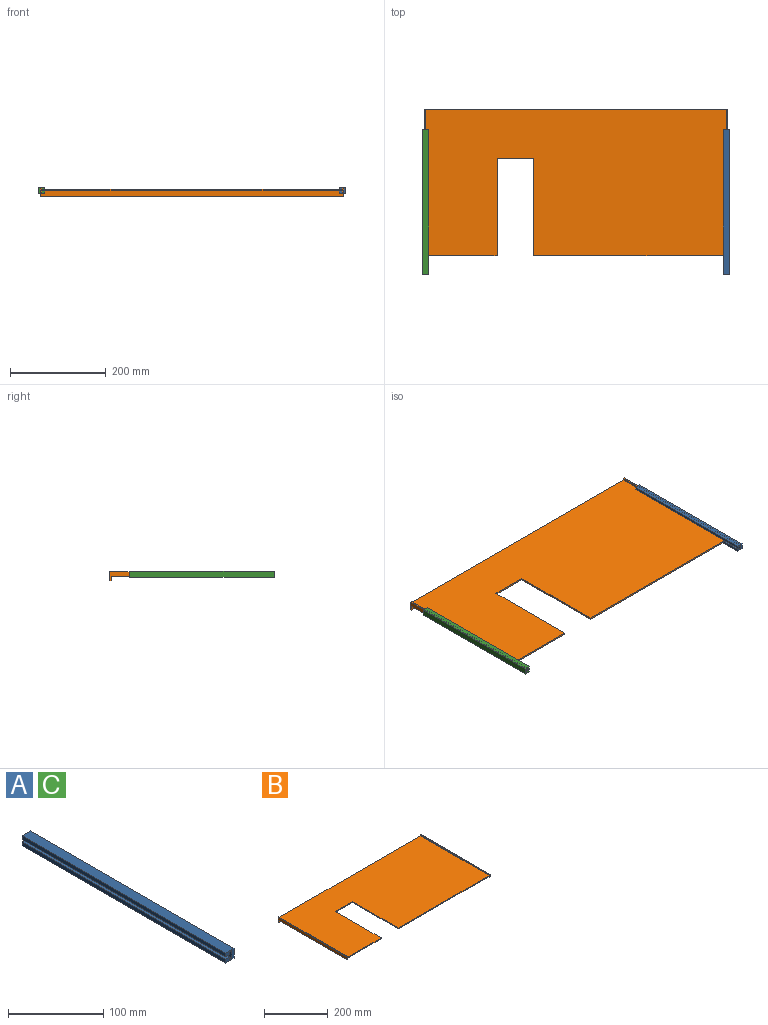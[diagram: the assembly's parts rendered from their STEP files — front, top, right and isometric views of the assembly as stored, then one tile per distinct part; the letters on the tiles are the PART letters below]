
ASSEMBLY  parts=3 mates=5
PART A: 14 faces, bbox 12.7x301.6x12.7 mm
  f0: plane 301.63x6.35mm, normal (0,0,1), area 1915.3mm2, adj f1,f11,f12,f13
  f1: plane 301.63x4.76mm, normal (-1,0,0), area 1436.5mm2, adj f0,f2,f12,f13
  f2: plane 301.63x12.7mm, normal (0,0,-1), area 3830.6mm2, adj f1,f3,f12,f13
  f3: plane 301.63x12.7mm, normal (1,0,0), area 3830.6mm2, adj f2,f4,f12,f13
  f4: plane 301.63x12.7mm, normal (0,0,1), area 3830.6mm2, adj f3,f5,f12,f13
  f5: plane 301.63x4.76mm, normal (-1,0,0), area 1436.5mm2, adj f4,f6,f12,f13
  f6: plane 301.63x6.35mm, normal (0,0,-1), area 1915.3mm2, adj f5,f7,f12,f13
  f7: plane 301.63x3.19mm, normal (1,0,0), area 961.5mm2, adj f6,f8,f12,f13
  f8: plane 301.63x3.18mm, normal (0,0,-1), area 957.7mm2, adj f7,f9,f12,f13
  f9: plane 301.63x9.55mm, normal (-1,0,0), area 2880.6mm2, adj f8,f10,f12,f13
  f10: plane 301.63x3.18mm, normal (0,0,1), area 957.7mm2, adj f9,f11,f12,f13
  f11: plane 301.63x3.19mm, normal (1,0,0), area 961.5mm2, adj f0,f10,f12,f13
  f12: plane 12.7x12.7mm, normal (0,-1,0), area 110.8mm2, adj f0,f1,f2,f3,f4,f5,f6,f7
  f13: plane 12.7x12.7mm, normal (0,1,0), area 110.8mm2, adj f0,f1,f2,f3,f4,f5,f6,f7
PART B: 20 faces, bbox 635x304.8x19.1 mm
  f0: plane 628.65x304.8mm, normal (0,0,1), area 176128.7mm2, adj f3,f4,f5,f6,f7,f9,f12,f16
  f1: plane 628.65x301.63mm, normal (0,0,-1), area 174132.7mm2, adj f3,f4,f5,f6,f7,f11,f15,f18
  f2: plane 304.8x19.05mm, normal (-1,0,0), area 2933.5mm2, adj f3,f9,f10,f13,f18,f19
  f3: plane 152.4x9.53mm, normal (0,-1,0), area 504mm2, adj f0,f1,f2,f4,f10,f11,f12,f13
  f4: plane 203.2x3.18mm, normal (1,0,0), area 645.2mm2, adj f0,f1,f3,f5
  f5: plane 76.2x3.18mm, normal (0,-1,0), area 241.9mm2, adj f0,f1,f4,f6
  f6: plane 203.2x3.18mm, normal (-1,0,0), area 645.2mm2, adj f0,f1,f5,f7
  f7: plane 406.4x9.53mm, normal (0,-1,0), area 1310.5mm2, adj f0,f1,f6,f8,f14,f15,f16,f17
  f8: plane 304.8x19.05mm, normal (1,0,0), area 2933.5mm2, adj f7,f9,f14,f17,f18,f19
  f9: plane 635x19.05mm, normal (0,1,0), area 10100.8mm2, adj f0,f2,f8,f12,f13,f16,f17,f19
  f10: plane 301.63x3.18mm, normal (0,0,-1), area 957.7mm2, adj f2,f3,f11,f18
  f11: plane 301.63x3.18mm, normal (1,0,0), area 957.7mm2, adj f1,f3,f10,f18
  f12: plane 304.8x3.18mm, normal (1,0,0), area 967.7mm2, adj f0,f3,f9,f13
  f13: plane 304.8x3.18mm, normal (0,0,1), area 967.7mm2, adj f2,f3,f9,f12
  f14: plane 301.63x3.18mm, normal (0,0,-1), area 957.7mm2, adj f7,f8,f15,f18
  f15: plane 301.63x3.18mm, normal (-1,0,0), area 957.7mm2, adj f1,f7,f14,f18
  f16: plane 304.8x3.18mm, normal (-1,0,0), area 967.7mm2, adj f0,f7,f9,f17
  f17: plane 304.8x3.18mm, normal (0,0,1), area 967.7mm2, adj f7,f8,f9,f16
  f18: plane 635x12.7mm, normal (0,-1,0), area 8044.3mm2, adj f1,f2,f8,f10,f11,f14,f15,f19
  f19: plane 635x3.18mm, normal (0,0,-1), area 2016.1mm2, adj f2,f8,f9,f18
PART C: same geometry as A
PLACE A t=(583.36,126.47,-6.77)mm fixed
PLACE B t=(14.8,-87.36,-0.42)mm
PLACE C rot(axis=(0,1,0),180deg) t=(-32.59,126.47,5.93)mm
MATE parallel C.f12 <-> A.f12  axis (0,-1,0) through (-35.76,-175.16,1.17)mm
MATE planar C.f6 <-> B.f1  axis (0,0,1) through (-35.76,-24.35,-2.01)mm
MATE planar C.f9 <-> B.f2  axis (1,0,0) through (-42.11,-24.35,-0.42)mm
MATE planar A.f9 <-> B.f8  axis (-1,0,0) through (592.89,-175.16,4.35)mm
MATE planar A.f0 <-> B.f1  axis (0,0,1) through (586.54,-24.35,-2.01)mm
